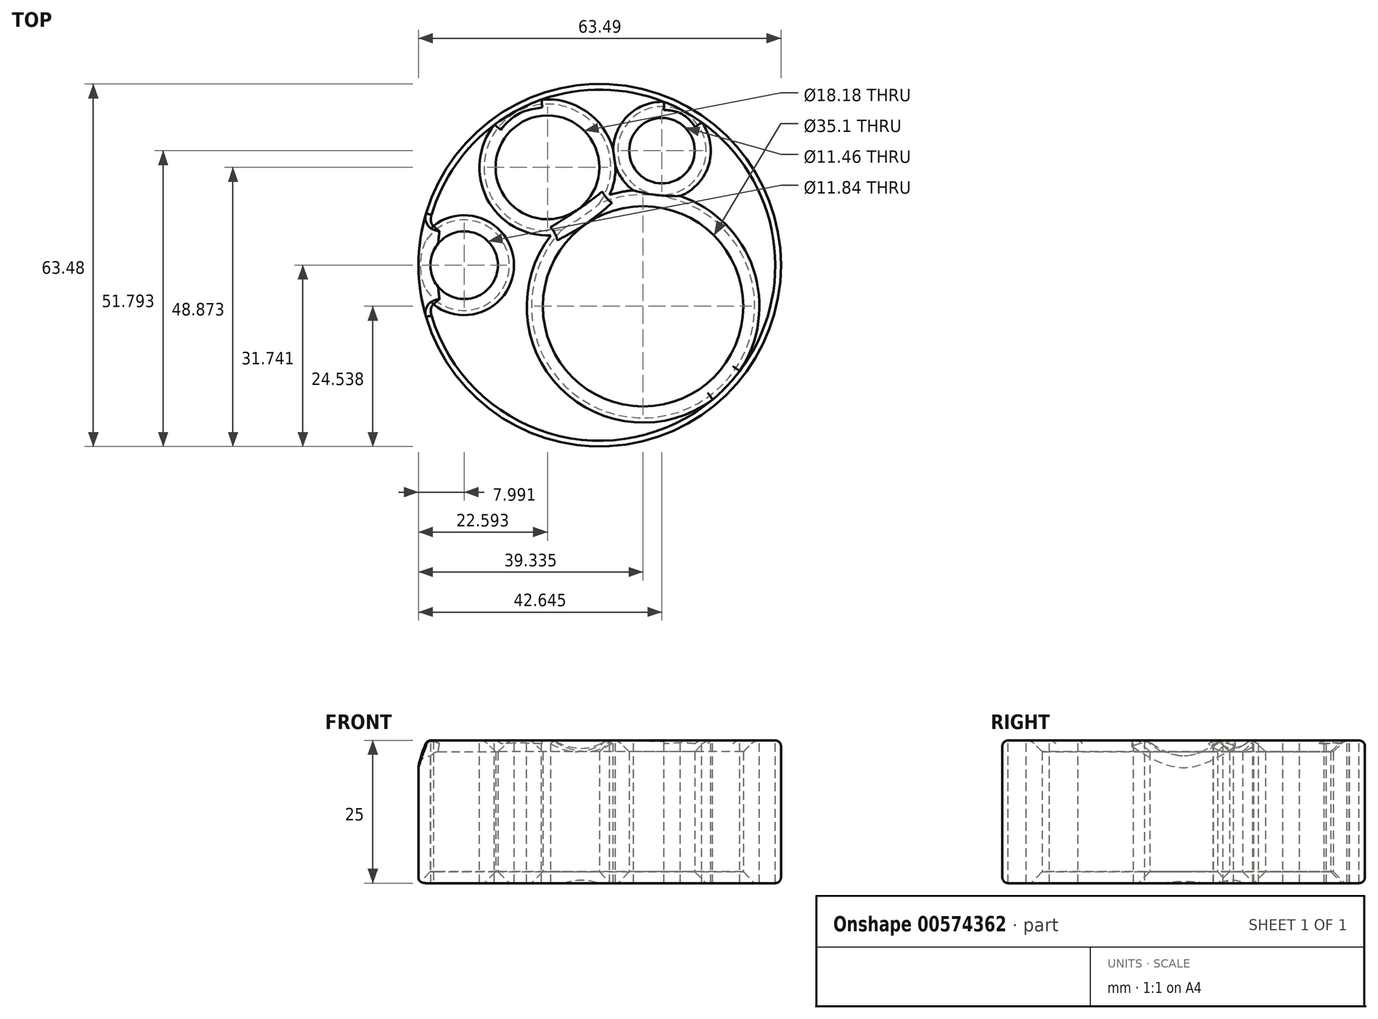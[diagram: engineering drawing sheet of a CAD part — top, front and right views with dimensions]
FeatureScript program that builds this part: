
annotation { "Feature Type Name" : "Feature", "Feature Type Description" : "" }
export const myFeature = defineFeature(function(context is Context, id is Id, definition is map)
    precondition{}
    {
        {
            var Q0;
            Q0=qCreatedBy(makeId("Top.planeOp"),FACE);
            var sketch = newSketch(context, id + "F0", { "sketchPlane" : qUnion([Q0])});
            skCircle(sketch, "E0", {"center": v(-41.86, 38.06) * mm, "radius": 31.74 * mm});
            skCircle(sketch, "E1", {"center": v(-51, 55.2) * mm, "radius": 9.09 * mm});
            skCircle(sketch, "E2", {"center": v(-34.26, 30.86) * mm, "radius": 17.55 * mm});
            skCircle(sketch, "E3", {"center": v(-30.95, 58.11) * mm, "radius": 5.73 * mm});
            skCircle(sketch, "E4", {"center": v(-65.6, 38.06) * mm, "radius": 5.92 * mm});
            skSolve(sketch);
        }
        {
            var Q0;
            Q0=makeQuery(id+"F0.imprint","IMPRINT",FACE,{"disambiguationData":[TD([[makeQuery(id+"F0.imprint","IMPRINT",EDGE,{"derivedFrom":sQuery(id+"F0.wireOp",EDGE,"E0")}),1.0]])]});
            extrude(context, id + "F1", {"entities" : qUnion([Q0]), "depth" : 25 * mm, "offsetDistance" : 25 * mm});
        }
        {
            var Q0;
            Q0=makeQuery(id+"F1.opExtrude","CAP_EDGE",EDGE,{"disambiguationData":[OSD([sQuery(id+"F0.wireOp",EDGE,"E0")])],"isStart":false});
            var Q1;
            Q1=makeQuery(id+"F1.opExtrude","CAP_EDGE",EDGE,{"disambiguationData":[OSD([sQuery(id+"F0.wireOp",EDGE,"E0")])],"isStart":true});
            fillet(context, id + "F2", {"entities" : qUnion([Q0, Q1]), "radius" : 1 * mm, "tangentPropagation" : true, "allowEdgeOverflow" : false});
        }
        {
            var Q0;
            Q0=makeQuery(id+"F1.opExtrude","CAP_EDGE",EDGE,{"disambiguationData":[OSD([sQuery(id+"F0.wireOp",EDGE,"E1")])],"isStart":false});
            var Q1;
            Q1=makeQuery(id+"F1.opExtrude","CAP_EDGE",EDGE,{"disambiguationData":[OSD([sQuery(id+"F0.wireOp",EDGE,"E3")])],"isStart":false});
            var Q2;
            Q2=makeQuery(id+"F1.opExtrude","CAP_EDGE",EDGE,{"disambiguationData":[OSD([sQuery(id+"F0.wireOp",EDGE,"E4")])],"isStart":false});
            var Q3;
            Q3=makeQuery(id+"F1.opExtrude","CAP_EDGE",EDGE,{"disambiguationData":[OSD([sQuery(id+"F0.wireOp",EDGE,"E2")])],"isStart":false});
            var Q4;
            Q4=makeQuery(id+"F1.opExtrude","CAP_EDGE",EDGE,{"disambiguationData":[OSD([sQuery(id+"F0.wireOp",EDGE,"E1")])],"isStart":true});
            var Q5;
            Q5=makeQuery(id+"F1.opExtrude","CAP_EDGE",EDGE,{"disambiguationData":[OSD([sQuery(id+"F0.wireOp",EDGE,"E4")])],"isStart":true});
            var Q6;
            Q6=makeQuery(id+"F1.opExtrude","CAP_EDGE",EDGE,{"disambiguationData":[OSD([sQuery(id+"F0.wireOp",EDGE,"E3")])],"isStart":true});
            var Q7;
            Q7=makeQuery(id+"F1.opExtrude","CAP_EDGE",EDGE,{"disambiguationData":[OSD([sQuery(id+"F0.wireOp",EDGE,"E2")])],"isStart":true});
            chamfer(context, id + "F3", {"entities" : qUnion([Q0, Q1, Q2, Q3, Q4, Q5, Q6, Q7]), "width" : 2 * mm, "tangentPropagation" : true});
        }
        {
            var Q0;
            Q0=makeQuery(id+"F3.opChamfer","BLEND_EDGE",EDGE,{"blendedFrom":[makeQuery(id+"F1.opExtrude","CAP_EDGE",EDGE,{"disambiguationData":[OSD([sQuery(id+"F0.wireOp",EDGE,"E1")])],"isStart":false}),makeQuery(id+"F1.opExtrude","CAP_EDGE",EDGE,{"disambiguationData":[OSD([sQuery(id+"F0.wireOp",EDGE,"E2")])],"isStart":false})],"blendedInto":[]});
            var Q1;
            {var subQ0=sQuery(id+"F0.wireOp",EDGE,"E1");Q1=makeQuery(id+"F3.opChamfer","BLEND_EDGE",EDGE,{"blendedFrom":[makeQuery(id+"F1.opExtrude","CAP_EDGE",EDGE,{"disambiguationData":[OSD([subQ0])],"isStart":false}),makeQuery(id+"F1.opExtrude","CAP_FACE",FACE,{"disambiguationData":[OSD([sQuery(id+"F0.wireOp",EDGE,"E0"),subQ0,sQuery(id+"F0.wireOp",EDGE,"E2"),sQuery(id+"F0.wireOp",EDGE,"E3"),sQuery(id+"F0.wireOp",EDGE,"E4")])],"isStart":false})],"blendedInto":[makeQuery(id+"F1.opExtrude","CAP_FACE",FACE,{"disambiguationData":[OSD([sQuery(id+"F0.wireOp",EDGE,"E0"),subQ0,sQuery(id+"F0.wireOp",EDGE,"E2"),sQuery(id+"F0.wireOp",EDGE,"E3"),sQuery(id+"F0.wireOp",EDGE,"E4")])],"isStart":false})]});}
            var Q2;
            {var subQ0=sQuery(id+"F0.wireOp",EDGE,"E2");Q2=makeQuery(id+"F3.opChamfer","BLEND_EDGE",EDGE,{"blendedFrom":[makeQuery(id+"F1.opExtrude","CAP_EDGE",EDGE,{"disambiguationData":[OSD([subQ0])],"isStart":false}),makeQuery(id+"F1.opExtrude","CAP_FACE",FACE,{"disambiguationData":[OSD([sQuery(id+"F0.wireOp",EDGE,"E0"),sQuery(id+"F0.wireOp",EDGE,"E1"),subQ0,sQuery(id+"F0.wireOp",EDGE,"E3"),sQuery(id+"F0.wireOp",EDGE,"E4")])],"isStart":false})],"blendedInto":[makeQuery(id+"F1.opExtrude","CAP_FACE",FACE,{"disambiguationData":[OSD([sQuery(id+"F0.wireOp",EDGE,"E0"),sQuery(id+"F0.wireOp",EDGE,"E1"),subQ0,sQuery(id+"F0.wireOp",EDGE,"E3"),sQuery(id+"F0.wireOp",EDGE,"E4")])],"isStart":false})]});}
            var Q3;
            {var subQ0=sQuery(id+"F0.wireOp",EDGE,"E3");Q3=makeQuery(id+"F3.opChamfer","BLEND_EDGE",EDGE,{"blendedFrom":[makeQuery(id+"F1.opExtrude","CAP_EDGE",EDGE,{"disambiguationData":[OSD([subQ0])],"isStart":false}),makeQuery(id+"F1.opExtrude","CAP_FACE",FACE,{"disambiguationData":[OSD([sQuery(id+"F0.wireOp",EDGE,"E0"),sQuery(id+"F0.wireOp",EDGE,"E1"),sQuery(id+"F0.wireOp",EDGE,"E2"),subQ0,sQuery(id+"F0.wireOp",EDGE,"E4")])],"isStart":false})],"blendedInto":[makeQuery(id+"F1.opExtrude","CAP_FACE",FACE,{"disambiguationData":[OSD([sQuery(id+"F0.wireOp",EDGE,"E0"),sQuery(id+"F0.wireOp",EDGE,"E1"),sQuery(id+"F0.wireOp",EDGE,"E2"),subQ0,sQuery(id+"F0.wireOp",EDGE,"E4")])],"isStart":false})]});}
            var Q4;
            {var subQ0=sQuery(id+"F0.wireOp",EDGE,"E4");Q4=makeQuery(id+"F3.opChamfer","BLEND_EDGE",EDGE,{"blendedFrom":[makeQuery(id+"F1.opExtrude","CAP_EDGE",EDGE,{"disambiguationData":[OSD([subQ0])],"isStart":false}),makeQuery(id+"F1.opExtrude","CAP_FACE",FACE,{"disambiguationData":[OSD([sQuery(id+"F0.wireOp",EDGE,"E0"),sQuery(id+"F0.wireOp",EDGE,"E1"),sQuery(id+"F0.wireOp",EDGE,"E2"),sQuery(id+"F0.wireOp",EDGE,"E3"),subQ0])],"isStart":false})],"blendedInto":[makeQuery(id+"F1.opExtrude","CAP_FACE",FACE,{"disambiguationData":[OSD([sQuery(id+"F0.wireOp",EDGE,"E0"),sQuery(id+"F0.wireOp",EDGE,"E1"),sQuery(id+"F0.wireOp",EDGE,"E2"),sQuery(id+"F0.wireOp",EDGE,"E3"),subQ0])],"isStart":false})]});}
            fillet(context, id + "F4", {"entities" : qUnion([Q0, Q1, Q2, Q3, Q4]), "radius" : 2 * mm, "tangentPropagation" : true, "allowEdgeOverflow" : false});
        }
        {
            var Q0;
            Q0=makeQuery(id+"F4.opFillet","SPLIT",FACE,{"disambiguationData":[OD(3.0)],"derivedFrom":makeQuery(id+"F1.opExtrude","CAP_FACE",FACE,{"disambiguationData":[OSD([sQuery(id+"F0.wireOp",EDGE,"E0"),sQuery(id+"F0.wireOp",EDGE,"E1"),sQuery(id+"F0.wireOp",EDGE,"E2"),sQuery(id+"F0.wireOp",EDGE,"E3"),sQuery(id+"F0.wireOp",EDGE,"E4")])],"isStart":false})});
            var Q1;
            Q1=makeQuery(id+"F4.opFillet","SPLIT",FACE,{"disambiguationData":[OD(2.0)],"derivedFrom":makeQuery(id+"F1.opExtrude","CAP_FACE",FACE,{"disambiguationData":[OSD([sQuery(id+"F0.wireOp",EDGE,"E0"),sQuery(id+"F0.wireOp",EDGE,"E1"),sQuery(id+"F0.wireOp",EDGE,"E2"),sQuery(id+"F0.wireOp",EDGE,"E3"),sQuery(id+"F0.wireOp",EDGE,"E4")])],"isStart":false})});
            var Q2;
            Q2=makeQuery(id+"F4.opFillet","SPLIT",FACE,{"disambiguationData":[OD(0.0)],"derivedFrom":makeQuery(id+"F1.opExtrude","CAP_FACE",FACE,{"disambiguationData":[OSD([sQuery(id+"F0.wireOp",EDGE,"E0"),sQuery(id+"F0.wireOp",EDGE,"E1"),sQuery(id+"F0.wireOp",EDGE,"E2"),sQuery(id+"F0.wireOp",EDGE,"E3"),sQuery(id+"F0.wireOp",EDGE,"E4")])],"isStart":false})});
            var Q3;
            Q3=makeQuery(id+"F4.opFillet","SPLIT",FACE,{"disambiguationData":[OD(1.0)],"derivedFrom":makeQuery(id+"F1.opExtrude","CAP_FACE",FACE,{"disambiguationData":[OSD([sQuery(id+"F0.wireOp",EDGE,"E0"),sQuery(id+"F0.wireOp",EDGE,"E1"),sQuery(id+"F0.wireOp",EDGE,"E2"),sQuery(id+"F0.wireOp",EDGE,"E3"),sQuery(id+"F0.wireOp",EDGE,"E4")])],"isStart":false})});
            extrude(context, id + "F5", {"entities" : qUnion([Q0, Q1, Q2, Q3]), "operationType" : NewBodyOperationType.REMOVE, "oppositeDirection" : true, "depth" : 30 * mm, "offsetDistance" : 25 * mm});
        }
    });
